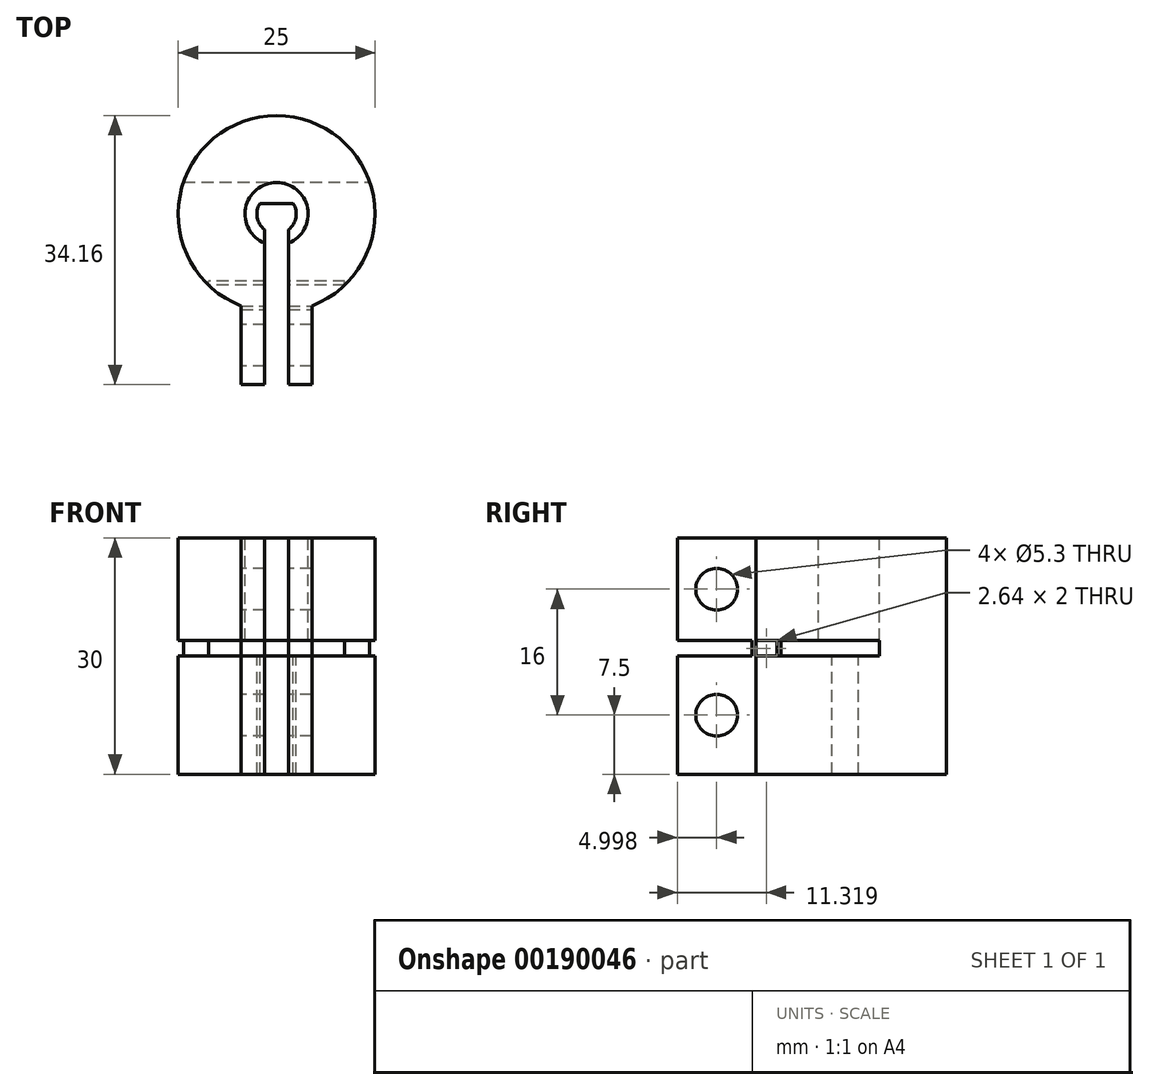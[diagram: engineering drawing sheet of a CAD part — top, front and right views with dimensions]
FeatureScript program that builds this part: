
annotation { "Feature Type Name" : "Feature", "Feature Type Description" : "" }
export const myFeature = defineFeature(function(context is Context, id is Id, definition is map)
    precondition{}
    {
        {
            var Q0;
            Q0=qCreatedBy(makeId("Top.planeOp"),FACE);
            var sketch = newSketch(context, id + "F0", { "sketchPlane" : qUnion([Q0])});
            skCircle(sketch, "E0", {"center": v(0, 0) * mm, "radius": 12.5 * mm});
            skSolve(sketch);
        }
        {
            var Q0;
            Q0 = qSketchRegion(id + "F0", true);
            extrude(context, id + "F1", {"entities" : qUnion([Q0]), "depth" : 30 * mm});
        }
        {
            var Q0;
            Q0=makeQuery(id+"F1.opExtrude","CAP_FACE",FACE,{"disambiguationData":[OSD([sQuery(id+"F0.wireOp",EDGE,"E0")])],"isStart":false});
            var sketch = newSketch(context, id + "F2", { "sketchPlane" : qUnion([Q0])});
            skCircle(sketch, "E1", {"center": v(0, 0) * mm, "radius": 2.5 * mm});
            skLineSegment(sketch, "E2", {"start": v(-2.1, 1.35) * mm, "end": v(2.1, 1.35) * mm});
            skSolve(sketch);
        }
        {
            var Q0;
            {var subQ0=sQuery(id+"F2.wireOp",EDGE,"E2");Q0=makeQuery(id+"F2.imprint","IMPRINT",FACE,{"disambiguationData":[TD([[makeQuery(id+"F2.imprint","IMPRINT",EDGE,{"derivedFrom":subQ0}),-1.0]])]});}
            extrude(context, id + "F3", {"entities" : qUnion([Q0]), "operationType" : NewBodyOperationType.REMOVE, "endBound" : BoundingType.THROUGH_ALL, "oppositeDirection" : true, "depth" : 25 * mm});
        }
        {
            var Q0;
            Q0=makeQuery(id+"F1.opExtrude","CAP_FACE",FACE,{"disambiguationData":[OSD([sQuery(id+"F0.wireOp",EDGE,"E0")])],"isStart":false});
            var sketch = newSketch(context, id + "F4", { "sketchPlane" : qUnion([Q0])});
            skCircle(sketch, "E3", {"center": v(0, 0) * mm, "radius": 4 * mm});
            skSolve(sketch);
        }
        {
            var Q0;
            Q0=makeQuery(id+"F4.imprint","IMPRINT",FACE,{"disambiguationData":[TD([[makeQuery(id+"F4.imprint","IMPRINT",EDGE,{"derivedFrom":sQuery(id+"F4.wireOp",EDGE,"E3")}),1.0]])]});
            extrude(context, id + "F5", {"entities" : qUnion([Q0]), "operationType" : NewBodyOperationType.REMOVE, "oppositeDirection" : true, "depth" : 15 * mm});
        }
        {
            var Q0;
            Q0=makeQuery(id+"F1.opExtrude","CAP_FACE",FACE,{"disambiguationData":[OSD([sQuery(id+"F0.wireOp",EDGE,"E0")])],"isStart":false});
            var sketch = newSketch(context, id + "F6", { "sketchPlane" : qUnion([Q0])});
            skLineSegment(sketch, "E4.bottom", {"start": v(-1.5, 0) * mm, "end": v(1.5, 0) * mm});
            skLineSegment(sketch, "E4.top", {"start": v(-1.5, -12.5) * mm, "end": v(1.5, -12.5) * mm});
            skLineSegment(sketch, "E4.left", {"start": v(-1.5, 0) * mm, "end": v(-1.5, -12.5) * mm});
            skLineSegment(sketch, "E4.right", {"start": v(1.5, 0) * mm, "end": v(1.5, -12.5) * mm});
            skPoint(sketch, "E5", {"position": v(0, 0) * mm});
            skSolve(sketch);
        }
        {
            var Q0;
            Q0 = qSketchRegion(id + "F6", true);
            extrude(context, id + "F7", {"entities" : qUnion([Q0]), "operationType" : NewBodyOperationType.REMOVE, "endBound" : BoundingType.THROUGH_ALL, "oppositeDirection" : true, "depth" : 25 * mm});
        }
        {
            var Q0;
            Q0=makeQuery(id+"F1.opExtrude","CAP_FACE",FACE,{"disambiguationData":[OSD([sQuery(id+"F0.wireOp",EDGE,"E0")])],"isStart":false});
            var sketch = newSketch(context, id + "F8", { "sketchPlane" : qUnion([Q0])});
            skLineSegment(sketch, "E6.bottom", {"start": v(-1.5, -21.66) * mm, "end": v(-4.5, -21.66) * mm});
            skLineSegment(sketch, "E6.top", {"start": v(-1.5, -11.66) * mm, "end": v(-4.5, -11.66) * mm});
            skLineSegment(sketch, "E6.left", {"start": v(-1.5, -21.66) * mm, "end": v(-1.5, -11.66) * mm});
            skLineSegment(sketch, "E6.right", {"start": v(-4.5, -21.66) * mm, "end": v(-4.5, -11.66) * mm});
            skLineSegment(sketch, "E7.bottom", {"start": v(1.5, -11.66) * mm, "end": v(4.5, -11.66) * mm});
            skLineSegment(sketch, "E7.top", {"start": v(1.5, -21.66) * mm, "end": v(4.5, -21.66) * mm});
            skLineSegment(sketch, "E7.left", {"start": v(1.5, -11.66) * mm, "end": v(1.5, -21.66) * mm});
            skLineSegment(sketch, "E7.right", {"start": v(4.5, -11.66) * mm, "end": v(4.5, -21.66) * mm});
            skSolve(sketch);
        }
        {
            var Q0;
            {var subQ0=sQuery(id+"F8.wireOp",EDGE,"E6.bottom");Q0=makeQuery(id+"F8.imprint","IMPRINT",FACE,{"disambiguationData":[TD([[makeQuery(id+"F8.imprint","IMPRINT",EDGE,{"derivedFrom":subQ0}),-1.0]])]});}
            var Q1;
            {var subQ0=sQuery(id+"F8.wireOp",EDGE,"E7.top");Q1=makeQuery(id+"F8.imprint","IMPRINT",FACE,{"disambiguationData":[TD([[makeQuery(id+"F8.imprint","IMPRINT",EDGE,{"derivedFrom":subQ0}),1.0]])]});}
            var Q2;
            Q2=makeQuery(id+"F1.opExtrude","CAP_FACE",FACE,{"disambiguationData":[OSD([sQuery(id+"F0.wireOp",EDGE,"E0")])],"isStart":true});
            extrude(context, id + "F9", {"entities" : qUnion([Q0, Q1]), "operationType" : NewBodyOperationType.ADD, "endBound" : BoundingType.UP_TO_SURFACE, "oppositeDirection" : true, "endBoundEntityFace" : qUnion([Q2]), "depth" : 25 * mm});
        }
        {
            var Q0;
            Q0=makeQuery(id+"F9.opExtrude","SWEPT_FACE",FACE,{"disambiguationData":[OSD([sQuery(id+"F8.wireOp",EDGE,"E7.top")])]});
            var sketch = newSketch(context, id + "F10", { "sketchPlane" : qUnion([Q0])});
            skLineSegment(sketch, "E8.bottom", {"start": v(-18.6, 17) * mm, "end": v(24.69, 17) * mm});
            skLineSegment(sketch, "E8.top", {"start": v(-18.6, 15) * mm, "end": v(24.69, 15) * mm});
            skLineSegment(sketch, "E8.left", {"start": v(-18.6, 17) * mm, "end": v(-18.6, 15) * mm});
            skLineSegment(sketch, "E8.right", {"start": v(24.69, 17) * mm, "end": v(24.69, 15) * mm});
            skSolve(sketch);
        }
        {
            var Q0;
            {var subQ0=sQuery(id+"F10.wireOp",EDGE,"E8.left");Q0=makeQuery(id+"F10.imprint","IMPRINT",FACE,{"disambiguationData":[TD([[makeQuery(id+"F10.imprint","IMPRINT",EDGE,{"derivedFrom":subQ0}),1.0]])]});}
            var Q1;
            {var subQ0=sQuery(id+"F10.wireOp",EDGE,"E8.bottom");var subQ1=sQuery(id+"F8.wireOp",EDGE,"E7.top");var subQ2=makeQuery(id+"F9.opExtrude","SWEPT_EDGE",EDGE,{"disambiguationData":[OSD([subQ1,sQuery(id+"F8.wireOp",EDGE,"E7.left")])]});var subQ3=makeQuery(id+"F10.imprint","INTERSECT",VERTEX,{"derivedFrom":[subQ2,subQ0]});Q1=makeQuery(id+"F10.imprint","IMPRINT",FACE,{"disambiguationData":[TD([[makeQuery(id+"F10.imprint","IMPRINT",EDGE,{"disambiguationData":[TD([[subQ3,-1.0]])],"derivedFrom":subQ0}),-1.0]])]});}
            var Q2;
            {var subQ0=sQuery(id+"F10.wireOp",EDGE,"E8.right");Q2=makeQuery(id+"F10.imprint","IMPRINT",FACE,{"disambiguationData":[TD([[makeQuery(id+"F10.imprint","IMPRINT",EDGE,{"derivedFrom":subQ0}),-1.0]])]});}
            var Q3;
            Q3=makeQuery(id+"F5.boolean.opBoolean","COPY",FACE,{"derivedFrom":makeQuery(id+"F5.opExtrude","SWEPT_FACE",FACE,{"disambiguationData":[OSD([sQuery(id+"F4.wireOp",EDGE,"E3")])]})});
            var Q4;
            Q4=makeQuery(id+"F1.opExtrude","SWEPT_BODY",BODY,{"disambiguationData":[OSD([sQuery(id+"F0.wireOp",EDGE,"E0")])]});
            extrude(context, id + "F11", {"entities" : qUnion([Q0, Q1, Q2]), "operationType" : NewBodyOperationType.REMOVE, "endBound" : BoundingType.SYMMETRIC, "oppositeDirection" : true, "endBoundEntityFace" : qUnion([Q3]), "endBoundEntityBody" : qUnion([Q4]), "depth" : 51.4 * mm});
        }
        {
            var Q0;
            {var subQ0=sQuery(id+"F8.wireOp",EDGE,"E6.right");var subQ2=sQuery(id+"F0.wireOp",EDGE,"E0");Q0=makeQuery(id+"F11.boolean.opBoolean","SPLIT",FACE,{"disambiguationData":[TD([makeQuery(id+"F1.opExtrude","CAP_FACE",FACE,{"disambiguationData":[OSD([subQ2])],"isStart":false})])],"derivedFrom":makeQuery(id+"F9.opExtrude","SWEPT_FACE",FACE,{"disambiguationData":[OSD([subQ0])]})});}
            var sketch = newSketch(context, id + "F12", { "sketchPlane" : qUnion([Q0])});
            skCircle(sketch, "E9", {"center": v(16.66, 23.5) * mm, "radius": 2.65 * mm});
            skPoint(sketch, "E10", {"position": v(16.66, 30) * mm});
            skPoint(sketch, "E11", {"position": v(21.66, 23.5) * mm});
            skPoint(sketch, "E12", {"position": v(21.66, 7.5) * mm});
            skCircle(sketch, "E13", {"center": v(16.66, 7.5) * mm, "radius": 2.65 * mm});
            skSolve(sketch);
        }
        {
            var Q0;
            Q0=makeQuery(id+"F12.imprint","IMPRINT",FACE,{"disambiguationData":[TD([[makeQuery(id+"F12.imprint","IMPRINT",EDGE,{"derivedFrom":sQuery(id+"F12.wireOp",EDGE,"E9")}),1.0]])]});
            var Q1;
            Q1=makeQuery(id+"F12.imprint","IMPRINT",FACE,{"disambiguationData":[TD([[makeQuery(id+"F12.imprint","IMPRINT",EDGE,{"derivedFrom":sQuery(id+"F12.wireOp",EDGE,"E13")}),1.0]])]});
            extrude(context, id + "F13", {"entities" : qUnion([Q0, Q1]), "operationType" : NewBodyOperationType.REMOVE, "endBound" : BoundingType.THROUGH_ALL, "oppositeDirection" : true, "depth" : 25 * mm});
        }
        {
            var Q0;
            Q0=makeQuery(id+"F11.boolean.opBoolean","MERGE",FACE,{"derivedFrom":[makeQuery(id+"F5.boolean.opBoolean","COPY",FACE,{"derivedFrom":makeQuery(id+"F5.opExtrude","CAP_FACE",FACE,{"disambiguationData":[OSD([sQuery(id+"F2.wireOp",EDGE,"E1"),sQuery(id+"F2.wireOp",EDGE,"E2"),sQuery(id+"F4.wireOp",EDGE,"E3")])],"isStart":false})}),makeQuery(id+"F11.opExtrude","SWEPT_FACE",FACE,{"disambiguationData":[OSD([sQuery(id+"F10.wireOp",EDGE,"E8.top")])]})]});
            var sketch = newSketch(context, id + "F14", { "sketchPlane" : qUnion([Q0])});
            skLineSegment(sketch, "E14.bottom", {"start": v(-4.5, -11.66) * mm, "end": v(4.5, -11.66) * mm});
            skLineSegment(sketch, "E14.top", {"start": v(-4.5, -12.16) * mm, "end": v(4.5, -12.16) * mm});
            skLineSegment(sketch, "E14.left", {"start": v(-4.5, -11.66) * mm, "end": v(-4.5, -12.16) * mm});
            skLineSegment(sketch, "E14.right", {"start": v(4.5, -11.66) * mm, "end": v(4.5, -12.16) * mm});
            skSolve(sketch);
        }
        {
            var Q0;
            {var subQ0=sQuery(id+"F14.wireOp",EDGE,"E14.left");Q0=makeQuery(id+"F14.imprint","IMPRINT",FACE,{"disambiguationData":[TD([[makeQuery(id+"F14.imprint","IMPRINT",EDGE,{"derivedFrom":subQ0}),-1.0]])]});}
            var Q1;
            {var subQ0=sQuery(id+"F14.wireOp",EDGE,"E14.right");Q1=makeQuery(id+"F14.imprint","IMPRINT",FACE,{"disambiguationData":[TD([[makeQuery(id+"F14.imprint","IMPRINT",EDGE,{"derivedFrom":subQ0}),-1.0]])]});}
            extrude(context, id + "F15", {"entities" : qUnion([Q0, Q1]), "operationType" : NewBodyOperationType.ADD, "endBound" : BoundingType.UP_TO_NEXT, "depth" : 25 * mm});
        }
        {
            var Q0;
            {var subQ6=sQuery(id+"F10.wireOp",EDGE,"E8.top");var subQ7=makeQuery(id+"F11.opExtrude","SWEPT_FACE",FACE,{"disambiguationData":[OSD([subQ6])]});var subQ8=makeQuery(id+"F1.opExtrude","SWEPT_FACE",FACE,{"disambiguationData":[OSD([sQuery(id+"F0.wireOp",EDGE,"E0")])]});var subQ15=sQuery(id+"F2.wireOp",EDGE,"E1");var subQ16=sQuery(id+"F2.wireOp",EDGE,"E2");Q0=makeQuery(id+"F15.boolean.opBoolean","SPLIT",FACE,{"disambiguationData":[TD([subQ8])],"derivedFrom":makeQuery(id+"F11.boolean.opBoolean","MERGE",FACE,{"derivedFrom":[makeQuery(id+"F5.boolean.opBoolean","COPY",FACE,{"derivedFrom":makeQuery(id+"F5.opExtrude","CAP_FACE",FACE,{"disambiguationData":[OSD([subQ15,subQ16,sQuery(id+"F4.wireOp",EDGE,"E3")])],"isStart":false})}),subQ7]})});}
            var sketch = newSketch(context, id + "F16", { "sketchPlane" : qUnion([Q0])});
            skLineSegment(sketch, "E15.bottom", {"start": v(8.65, -9.02) * mm, "end": v(-8.65, -9.02) * mm});
            skLineSegment(sketch, "E15.top", {"start": v(8.65, -8.52) * mm, "end": v(-8.65, -8.52) * mm});
            skLineSegment(sketch, "E15.left", {"start": v(8.65, -9.02) * mm, "end": v(8.65, -8.52) * mm});
            skLineSegment(sketch, "E15.right", {"start": v(-8.65, -9.02) * mm, "end": v(-8.65, -8.52) * mm});
            skSolve(sketch);
        }
        {
            var Q0;
            {var subQ0=sQuery(id+"F16.wireOp",EDGE,"E15.left");Q0=makeQuery(id+"F16.imprint","IMPRINT",FACE,{"disambiguationData":[TD([[makeQuery(id+"F16.imprint","IMPRINT",EDGE,{"derivedFrom":subQ0}),1.0]])]});}
            var Q1;
            {var subQ0=sQuery(id+"F16.wireOp",EDGE,"E15.right");Q1=makeQuery(id+"F16.imprint","IMPRINT",FACE,{"disambiguationData":[TD([[makeQuery(id+"F16.imprint","IMPRINT",EDGE,{"derivedFrom":subQ0}),-1.0]])]});}
            extrude(context, id + "F17", {"entities" : qUnion([Q0, Q1]), "operationType" : NewBodyOperationType.ADD, "endBound" : BoundingType.UP_TO_NEXT, "depth" : 25 * mm});
        }
    });
